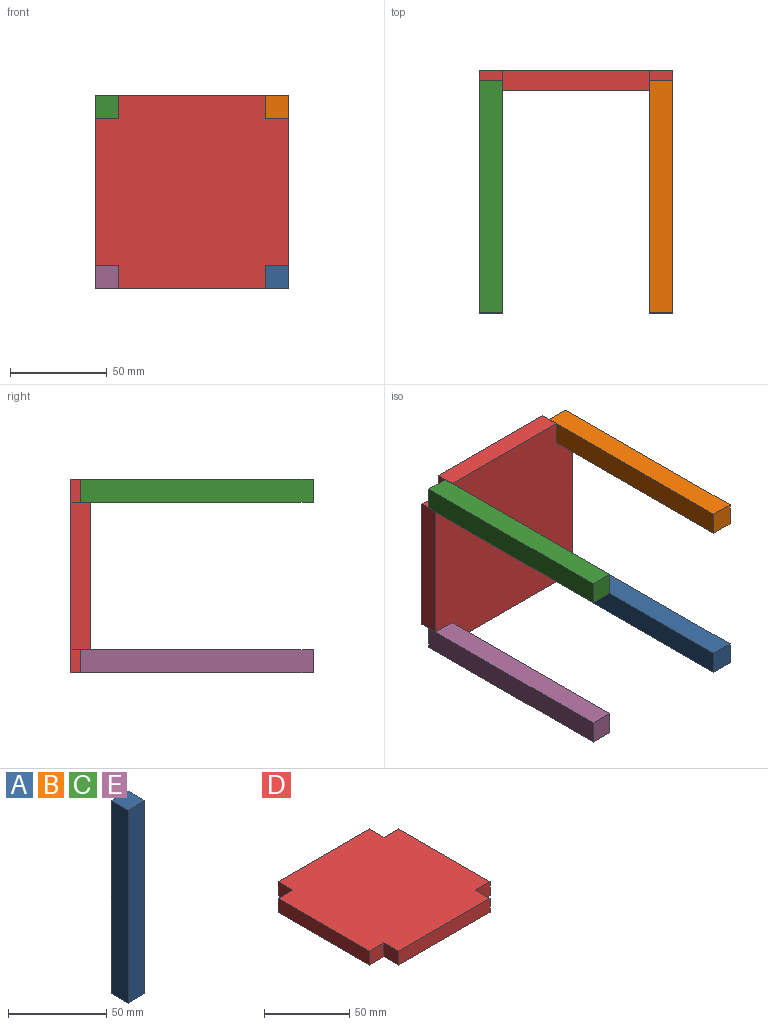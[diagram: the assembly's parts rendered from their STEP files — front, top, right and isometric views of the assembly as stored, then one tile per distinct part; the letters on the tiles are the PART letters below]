
ASSEMBLY  parts=5 mates=4
PART A: 6 faces, bbox 12x12x120 mm
  f0: plane 120x12mm, normal (-1,0,0), area 1440mm2, adj f1,f3,f4,f5
  f1: plane 120x12mm, normal (0,-1,0), area 1440mm2, adj f0,f2,f4,f5
  f2: plane 120x12mm, normal (1,0,0), area 1440mm2, adj f1,f3,f4,f5
  f3: plane 120x12mm, normal (0,1,0), area 1440mm2, adj f0,f2,f4,f5
  f4: plane 12x12mm, normal (0,0,-1), area 144mm2, adj f0,f1,f2,f3
  f5: plane 12x12mm, normal (0,0,1), area 144mm2, adj f0,f1,f2,f3
PART B: same geometry as A
PART C: same geometry as A
PART D: 14 faces, bbox 100x100x10 mm
  f0: plane 76x10mm, normal (-1,0,0), area 760mm2, adj f4,f5,f9,f11
  f1: plane 76x10mm, normal (0,-1,0), area 760mm2, adj f4,f5,f7,f10
  f2: plane 76x10mm, normal (1,0,0), area 760mm2, adj f4,f5,f6,f13
  f3: plane 76x10mm, normal (0,1,0), area 760mm2, adj f4,f5,f8,f12
  f4: plane 100x100mm, normal (0,0,1), area 9424mm2, adj f0,f1,f2,f3,f6,f7,f8,f9
  f5: plane 100x100mm, normal (0,0,-1), area 9424mm2, adj f0,f1,f2,f3,f6,f7,f8,f9
  f6: plane 12x10mm, normal (0,-1,0), area 120mm2, adj f2,f4,f5,f7
  f7: plane 12x10mm, normal (1,0,0), area 120mm2, adj f1,f4,f5,f6
  f8: plane 12x10mm, normal (-1,0,0), area 120mm2, adj f3,f4,f5,f9
  f9: plane 12x10mm, normal (0,1,0), area 120mm2, adj f0,f4,f5,f8
  f10: plane 12x10mm, normal (-1,0,0), area 120mm2, adj f1,f4,f5,f11
  f11: plane 12x10mm, normal (0,-1,0), area 120mm2, adj f0,f4,f5,f10
  f12: plane 12x10mm, normal (1,0,0), area 120mm2, adj f3,f4,f5,f13
  f13: plane 12x10mm, normal (0,1,0), area 120mm2, adj f2,f4,f5,f12
PART E: same geometry as A
PLACE A rot(axis=(0,-0.71,-0.71),180deg) t=(591.96,-686.33,384.14)mm
PLACE B rot(axis=(0.58,-0.58,0.58),120deg) t=(579.96,-806.33,460.14)mm
PLACE C rot(axis=(0,0.71,0.71),180deg) t=(503.96,-686.33,472.14)mm
PLACE D rot(axis=(0,-0.71,-0.71),180deg) t=(591.96,-691.33,472.14)mm
PLACE E rot(axis=(1,0,0),90deg) t=(491.96,-806.33,384.14)mm
MATE fastened A.f3 <-> D.f11  axis (0,0,1) through (585.96,-686.33,384.14)mm
MATE fastened E.f3 <-> D.f6  axis (0,0,1) through (497.96,-686.33,384.14)mm
MATE fastened C.f0 <-> D.f12  axis (1,0,0) through (503.96,-686.33,466.14)mm
MATE fastened B.f3 <-> D.f8  axis (-1,0,0) through (579.96,-686.33,466.14)mm
